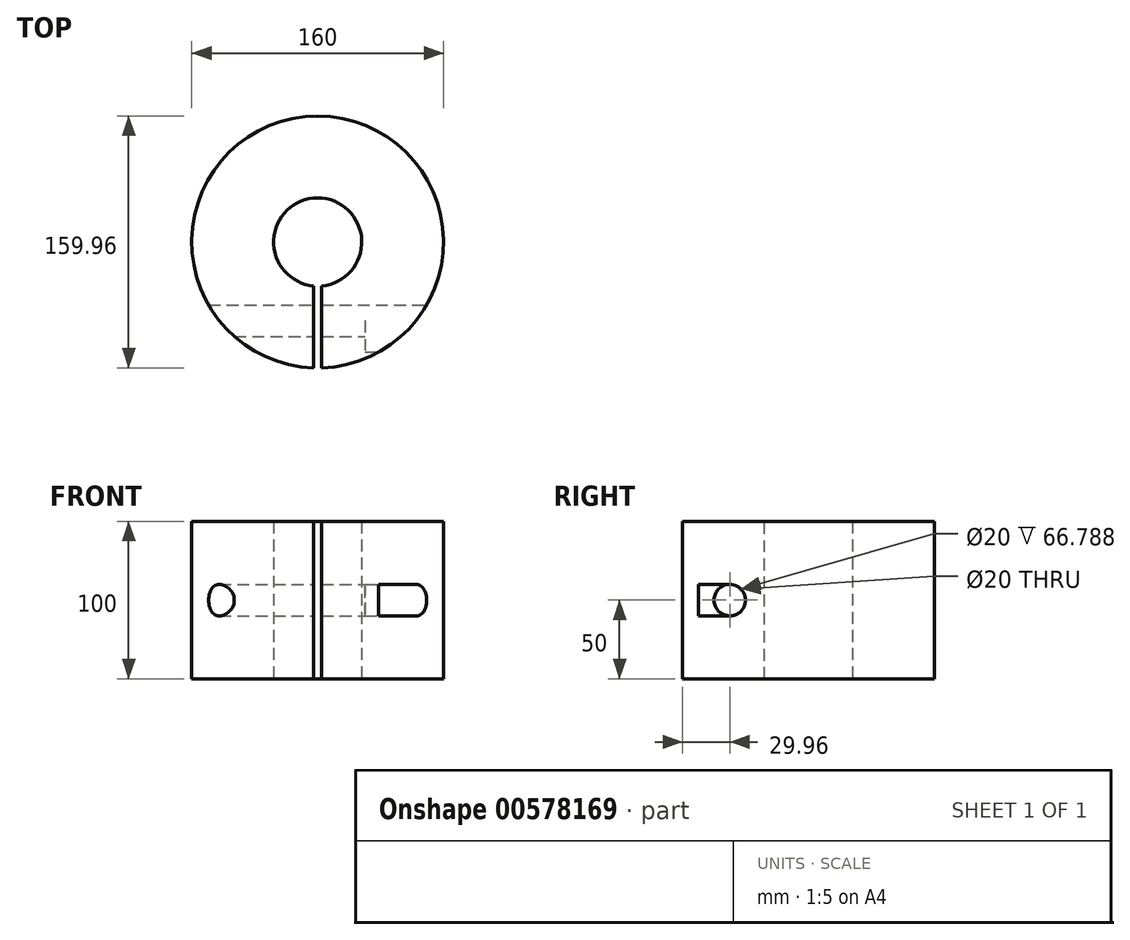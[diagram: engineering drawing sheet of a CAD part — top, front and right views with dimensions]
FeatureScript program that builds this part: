
annotation { "Feature Type Name" : "Feature", "Feature Type Description" : "" }
export const myFeature = defineFeature(function(context is Context, id is Id, definition is map)
    precondition{}
    {
        {
            var Q0;
            Q0=qCreatedBy(makeId("Top.planeOp"),FACE);
            var sketch = newSketch(context, id + "F0", { "sketchPlane" : qUnion([Q0])});
            skCircle(sketch, "E0", {"center": v(0, 0) * mm, "radius": 80 * mm});
            skCircle(sketch, "E1", {"center": v(0, 0) * mm, "radius": 28 * mm});
            skSolve(sketch);
        }
        {
            var Q0;
            Q0=makeQuery(id+"F0.imprint","IMPRINT",FACE,{"disambiguationData":[TD([[makeQuery(id+"F0.imprint","IMPRINT",EDGE,{"derivedFrom":sQuery(id+"F0.wireOp",EDGE,"E0")}),1.0]])]});
            extrude(context, id + "F1", {"entities" : qUnion([Q0]), "depth" : 100 * mm, "offsetDistance" : 25 * mm});
        }
        {
            var Q0;
            Q0=qCreatedBy(makeId("Right.planeOp"),FACE);
            var sketch = newSketch(context, id + "F2", { "sketchPlane" : qUnion([Q0])});
            skCircle(sketch, "E2", {"center": v(-50, 50) * mm, "radius": 10 * mm});
            skSolve(sketch);
        }
        {
            var Q0;
            Q0 = qSketchRegion(id + "F2", true);
            extrude(context, id + "F3", {"entities" : qUnion([Q0]), "operationType" : NewBodyOperationType.REMOVE, "endBound" : BoundingType.SYMMETRIC, "oppositeDirection" : true, "depth" : 500 * mm, "offsetDistance" : 25 * mm});
        }
        {
            var Q0;
            Q0=makeQuery(id+"F1.opExtrude","CAP_FACE",FACE,{"disambiguationData":[OSD([sQuery(id+"F0.wireOp",EDGE,"E0"),sQuery(id+"F0.wireOp",EDGE,"E1")])],"isStart":false});
            var sketch = newSketch(context, id + "F4", { "sketchPlane" : qUnion([Q0])});
            skLineSegment(sketch, "E3.bottom", {"start": v(-2.5, -21.85) * mm, "end": v(2.5, -21.85) * mm});
            skLineSegment(sketch, "E3.top", {"start": v(-2.5, -92.6) * mm, "end": v(2.5, -92.6) * mm});
            skLineSegment(sketch, "E3.left", {"start": v(-2.5, -21.85) * mm, "end": v(-2.5, -92.6) * mm});
            skLineSegment(sketch, "E3.right", {"start": v(2.5, -21.85) * mm, "end": v(2.5, -92.6) * mm});
            skSolve(sketch);
        }
        {
            var Q0;
            {var subQ0=sQuery(id+"F4.wireOp",EDGE,"E3.left");var subQ1=makeQuery(id+"F1.opExtrude","CAP_EDGE",EDGE,{"disambiguationData":[OSD([sQuery(id+"F0.wireOp",EDGE,"E0")])],"isStart":false});var subQ2=makeQuery(id+"F4.imprint","INTERSECT",VERTEX,{"derivedFrom":[subQ1,subQ0]});Q0=makeQuery(id+"F4.imprint","IMPRINT",FACE,{"disambiguationData":[TD([[makeQuery(id+"F4.imprint","IMPRINT",EDGE,{"disambiguationData":[TD([[subQ2,1.0]])],"derivedFrom":subQ0}),1.0]])]});}
            extrude(context, id + "F5", {"entities" : qUnion([Q0]), "operationType" : NewBodyOperationType.REMOVE, "endBound" : BoundingType.THROUGH_ALL, "oppositeDirection" : true, "depth" : 25 * mm, "offsetDistance" : 25 * mm});
        }
        {
            var Q0;
            Q0=qCreatedBy(makeId("Right.planeOp"),FACE);
            cPlane(context, id + "F6", {"entities" : qUnion([Q0]), "cplaneType" : CPlaneType.OFFSET, "offset" : 80 * mm, "width" : 150 * mm, "height" : 150 * mm});
        }
        {
            var Q0;
            Q0=qCreatedBy(id+"F6.planeOp",FACE);
            var sketch = newSketch(context, id + "F7", { "sketchPlane" : qUnion([Q0])});
            skCircle(sketch, "E4", {"center": v(-50, 50) * mm, "radius": 10 * mm});
            skLineSegment(sketch, "E5.bottom", {"start": v(-50, 40) * mm, "end": v(-70, 40) * mm});
            skLineSegment(sketch, "E5.top", {"start": v(-50, 60) * mm, "end": v(-70, 60) * mm});
            skLineSegment(sketch, "E5.left", {"start": v(-50, 40) * mm, "end": v(-50, 60) * mm});
            skLineSegment(sketch, "E5.right", {"start": v(-70, 40) * mm, "end": v(-70, 60) * mm});
            skSolve(sketch);
        }
        {
            var Q0;
            {var subQ1=sQuery(id+"F7.wireOp",EDGE,"E5.bottom");Q0=makeQuery(id+"F7.imprint","IMPRINT",FACE,{"disambiguationData":[TD([[makeQuery(id+"F7.imprint","IMPRINT",EDGE,{"derivedFrom":subQ1}),-1.0]])]});}
            extrude(context, id + "F8", {"entities" : qUnion([Q0]), "operationType" : NewBodyOperationType.REMOVE, "oppositeDirection" : true, "depth" : 50 * mm, "offsetDistance" : 25 * mm});
        }
    });
